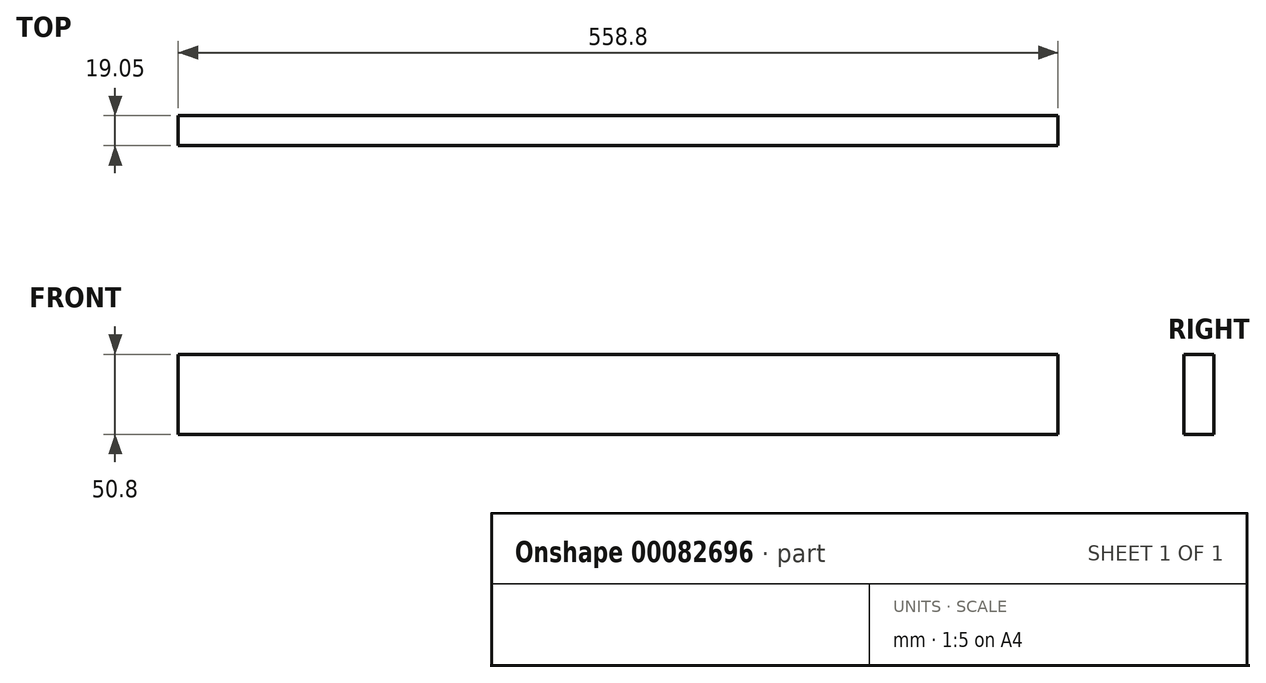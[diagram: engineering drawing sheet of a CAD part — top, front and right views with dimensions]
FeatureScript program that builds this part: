
annotation { "Feature Type Name" : "Feature", "Feature Type Description" : "" }
export const myFeature = defineFeature(function(context is Context, id is Id, definition is map)
    precondition{}
    {
        {
            var Q0;
            Q0=qCreatedBy(makeId("Front.planeOp"),FACE);
            var sketch = newSketch(context, id + "F0", { "sketchPlane" : qUnion([Q0])});
            skLineSegment(sketch, "E0.bottom", {"start": v(-340.78, -114.96) * mm, "end": v(218.02, -114.96) * mm});
            skLineSegment(sketch, "E0.top", {"start": v(-340.78, -165.76) * mm, "end": v(218.02, -165.76) * mm});
            skLineSegment(sketch, "E0.left", {"start": v(-340.78, -114.96) * mm, "end": v(-340.78, -165.76) * mm});
            skLineSegment(sketch, "E0.right", {"start": v(218.02, -114.96) * mm, "end": v(218.02, -165.76) * mm});
            skSolve(sketch);
        }
        {
            var Q0;
            Q0=qSketchRegion(id+"F0",true);
            extrude(context, id + "F1", {"entities" : qUnion([Q0]), "depth" : 19.05 * mm});
        }
    });
